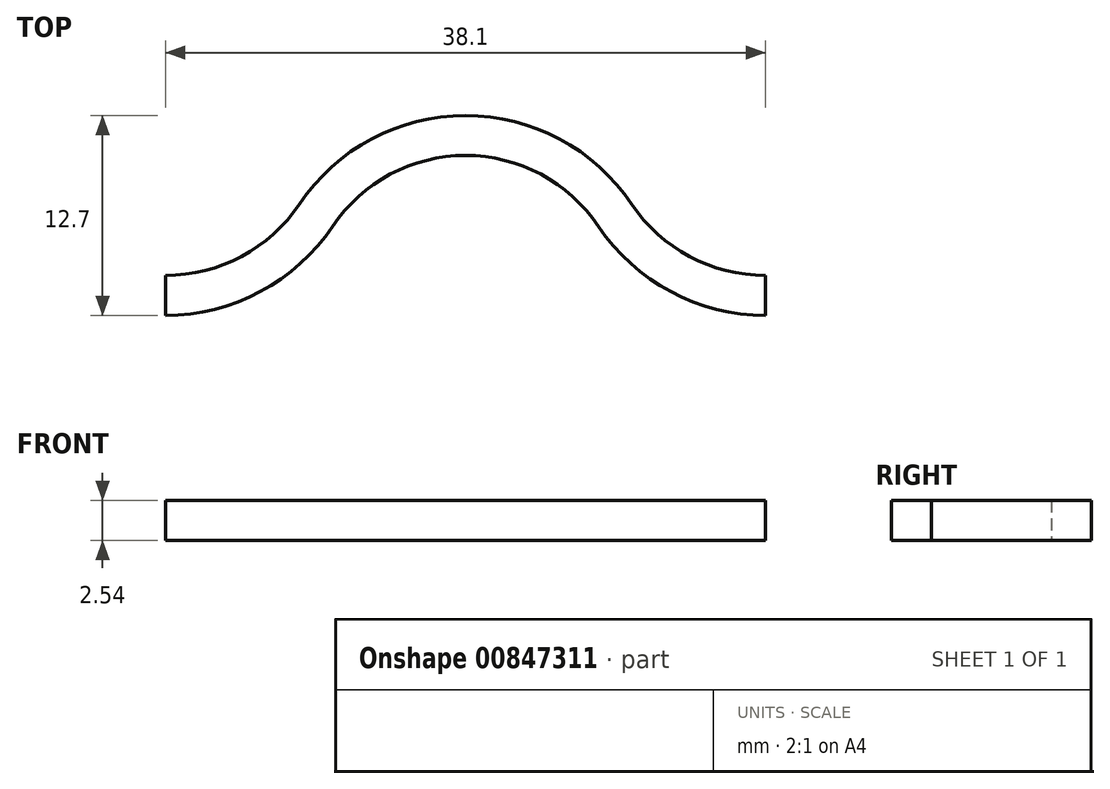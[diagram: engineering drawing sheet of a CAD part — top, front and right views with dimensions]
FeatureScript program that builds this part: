
annotation { "Feature Type Name" : "Feature", "Feature Type Description" : "" }
export const myFeature = defineFeature(function(context is Context, id is Id, definition is map)
    precondition{}
    {
        {
            var Q0;
            Q0=qCreatedBy(makeId("Top.planeOp"),FACE);
            var sketch = newSketch(context, id + "F0", { "sketchPlane" : qUnion([Q0])});
            skArc(sketch, "E0", {"start": v(8.44, 5.66) * mm, "mid": v(0, 10.16) * mm, "end": v(-8.44, 5.66) * mm});
            skArc(sketch, "E1", {"start": v(-19.05, 0) * mm, "mid": v(-13.04, 1.5) * mm, "end": v(-8.44, 5.66) * mm});
            skArc(sketch, "E2.MirrorCS", {"start": v(19.05, 0) * mm, "mid": v(13.04, 1.5) * mm, "end": v(8.44, 5.66) * mm});
            skArc(sketch, "E3.0", {"start": v(19.05, 2.54) * mm, "mid": v(14.23, 3.74) * mm, "end": v(10.55, 7.08) * mm});
            skArc(sketch, "E3.1", {"start": v(10.55, 7.08) * mm, "mid": v(0, 12.7) * mm, "end": v(-10.55, 7.08) * mm});
            skArc(sketch, "E3.2", {"start": v(-19.05, 2.54) * mm, "mid": v(-14.23, 3.74) * mm, "end": v(-10.55, 7.08) * mm});
            skLineSegment(sketch, "E4", {"start": v(-19.05, 0) * mm, "end": v(-19.05, 2.54) * mm});
            skLineSegment(sketch, "E5", {"start": v(19.05, 0) * mm, "end": v(19.05, 2.54) * mm});
            skSolve(sketch);
        }
        {
            var Q0;
            Q0 = qSketchRegion(id + "F0", true);
            extrude(context, id + "F1", {"entities" : qUnion([Q0]), "depth" : 2.54 * mm, "offsetDistance" : 25.4 * mm});
        }
    });
